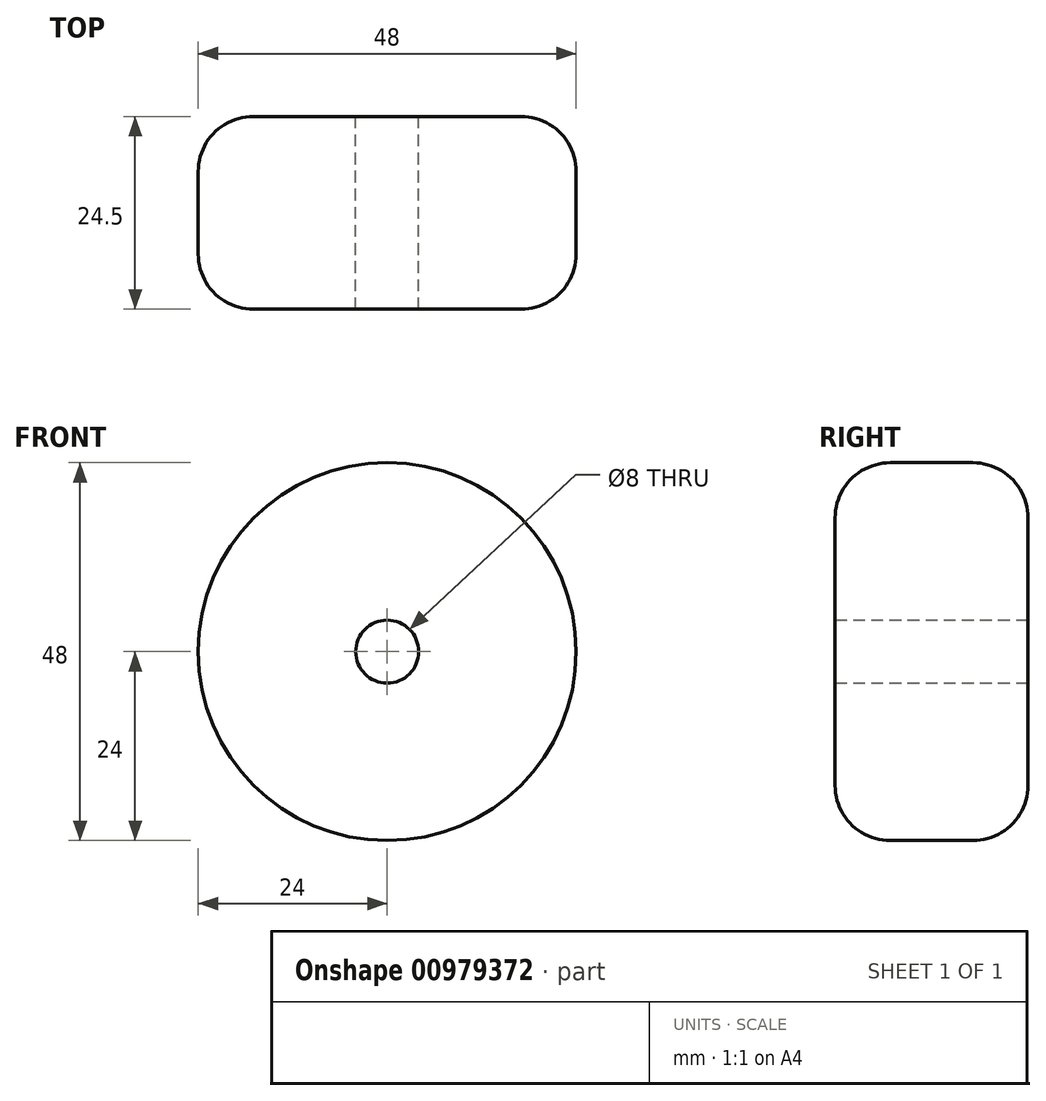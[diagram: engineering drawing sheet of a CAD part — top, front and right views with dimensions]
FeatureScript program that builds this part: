
annotation { "Feature Type Name" : "Feature", "Feature Type Description" : "" }
export const myFeature = defineFeature(function(context is Context, id is Id, definition is map)
    precondition{}
    {
        {
            var Q0;
            Q0=qCreatedBy(makeId("Front.planeOp"),FACE);
            var sketch = newSketch(context, id + "F0", { "sketchPlane" : qUnion([Q0])});
            skCircle(sketch, "E0", {"center": v(0, 0) * mm, "radius": 24 * mm});
            skCircle(sketch, "E1", {"center": v(0, 0) * mm, "radius": 4 * mm});
            skSolve(sketch);
        }
        {
            var Q0;
            Q0=makeQuery(id+"F0.imprint","IMPRINT",FACE,{"disambiguationData":[TD([[makeQuery(id+"F0.imprint","IMPRINT",EDGE,{"derivedFrom":sQuery(id+"F0.wireOp",EDGE,"E0")}),1.0]])]});
            extrude(context, id + "F1", {"entities" : qUnion([Q0]), "endBound" : BoundingType.SYMMETRIC, "depth" : 24.5 * mm, "offsetDistance" : 25 * mm});
        }
        {
            var Q0;
            Q0=makeQuery(id+"F1.opExtrude","CAP_EDGE",EDGE,{"disambiguationData":[OSD([sQuery(id+"F0.wireOp",EDGE,"E0")])],"isStart":false});
            var Q1;
            Q1=makeQuery(id+"F1.opExtrude","CAP_EDGE",EDGE,{"disambiguationData":[OSD([sQuery(id+"F0.wireOp",EDGE,"E0")])],"isStart":true});
            fillet(context, id + "F2", {"entities" : qUnion([Q0, Q1]), "radius" : 7 * mm, "tangentPropagation" : true, "allowEdgeOverflow" : false});
        }
    });
